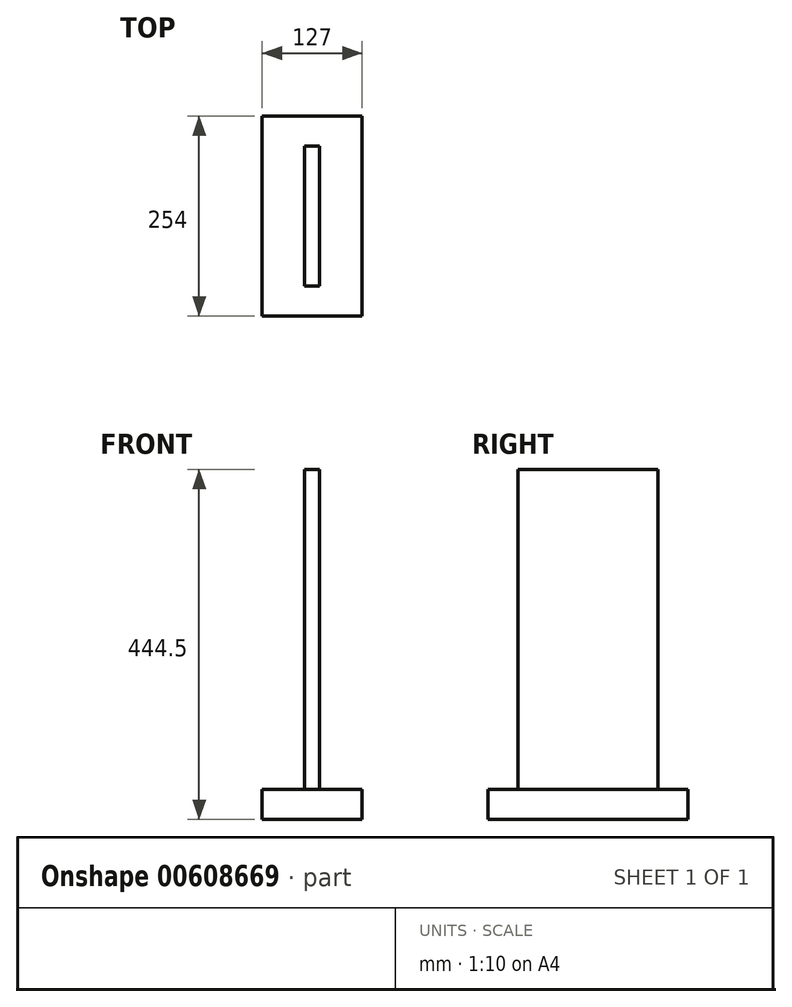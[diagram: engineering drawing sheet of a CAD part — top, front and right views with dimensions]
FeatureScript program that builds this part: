
annotation { "Feature Type Name" : "Feature", "Feature Type Description" : "" }
export const myFeature = defineFeature(function(context is Context, id is Id, definition is map)
    precondition{}
    {
        {
            var Q0;
            Q0=qCreatedBy(makeId("Right.planeOp"),FACE);
            var sketch = newSketch(context, id + "F0", { "sketchPlane" : qUnion([Q0])});
            skLineSegment(sketch, "E0.bottom", {"start": v(38.1, 88.9) * mm, "end": v(-38.1, 88.9) * mm});
            skLineSegment(sketch, "E0.top", {"start": v(38.1, 393.7) * mm, "end": v(-38.1, 393.7) * mm});
            skLineSegment(sketch, "E0.left", {"start": v(38.1, 88.9) * mm, "end": v(38.1, 393.7) * mm});
            skLineSegment(sketch, "E0.right", {"start": v(-38.1, 88.9) * mm, "end": v(-38.1, 393.7) * mm});
            skPoint(sketch, "E0.middle", {"position": v(0, 241.3) * mm});
            skLineSegment(sketch, "E1.bottom", {"start": v(88.9, 38.1) * mm, "end": v(-88.9, 38.1) * mm});
            skLineSegment(sketch, "E1.top", {"start": v(88.9, 444.5) * mm, "end": v(-88.9, 444.5) * mm});
            skLineSegment(sketch, "E1.left", {"start": v(88.9, 38.1) * mm, "end": v(88.9, 444.5) * mm});
            skLineSegment(sketch, "E1.right", {"start": v(-88.9, 38.1) * mm, "end": v(-88.9, 444.5) * mm});
            skLineSegment(sketch, "E2.bottom", {"start": v(-127, 0) * mm, "end": v(127, 0) * mm});
            skLineSegment(sketch, "E2.top", {"start": v(-127, 38.1) * mm, "end": v(127, 38.1) * mm});
            skLineSegment(sketch, "E2.left", {"start": v(-127, 0) * mm, "end": v(-127, 38.1) * mm});
            skLineSegment(sketch, "E2.right", {"start": v(127, 0) * mm, "end": v(127, 38.1) * mm});
            skPoint(sketch, "E2.middle", {"position": v(0, 19.05) * mm});
            skSolve(sketch);
        }
        {
            var Q0;
            Q0=makeQuery(id+"F0.imprint","IMPRINT",FACE,{"disambiguationData":[TD([[makeQuery(id+"F0.imprint","IMPRINT",EDGE,{"derivedFrom":sQuery(id+"F0.wireOp",EDGE,"E0.bottom")}),1.0]])]});
            var Q1;
            Q1=makeQuery(id+"F0.imprint","IMPRINT",FACE,{"disambiguationData":[TD([[makeQuery(id+"F0.imprint","IMPRINT",EDGE,{"derivedFrom":sQuery(id+"F0.wireOp",EDGE,"E0.bottom")}),-1.0]])]});
            extrude(context, id + "F1", {"entities" : qUnion([Q0, Q1]), "endBound" : BoundingType.SYMMETRIC, "depth" : 19.05 * mm, "offsetDistance" : 25.4 * mm});
        }
        {
            var Q0;
            Q0=makeQuery(id+"F0.imprint","IMPRINT",FACE,{"disambiguationData":[TD([[makeQuery(id+"F0.imprint","IMPRINT",EDGE,{"derivedFrom":sQuery(id+"F0.wireOp",EDGE,"E2.bottom")}),1.0]])]});
            extrude(context, id + "F2", {"entities" : qUnion([Q0]), "endBound" : BoundingType.SYMMETRIC, "depth" : 127 * mm, "offsetDistance" : 25.4 * mm});
        }
    });
